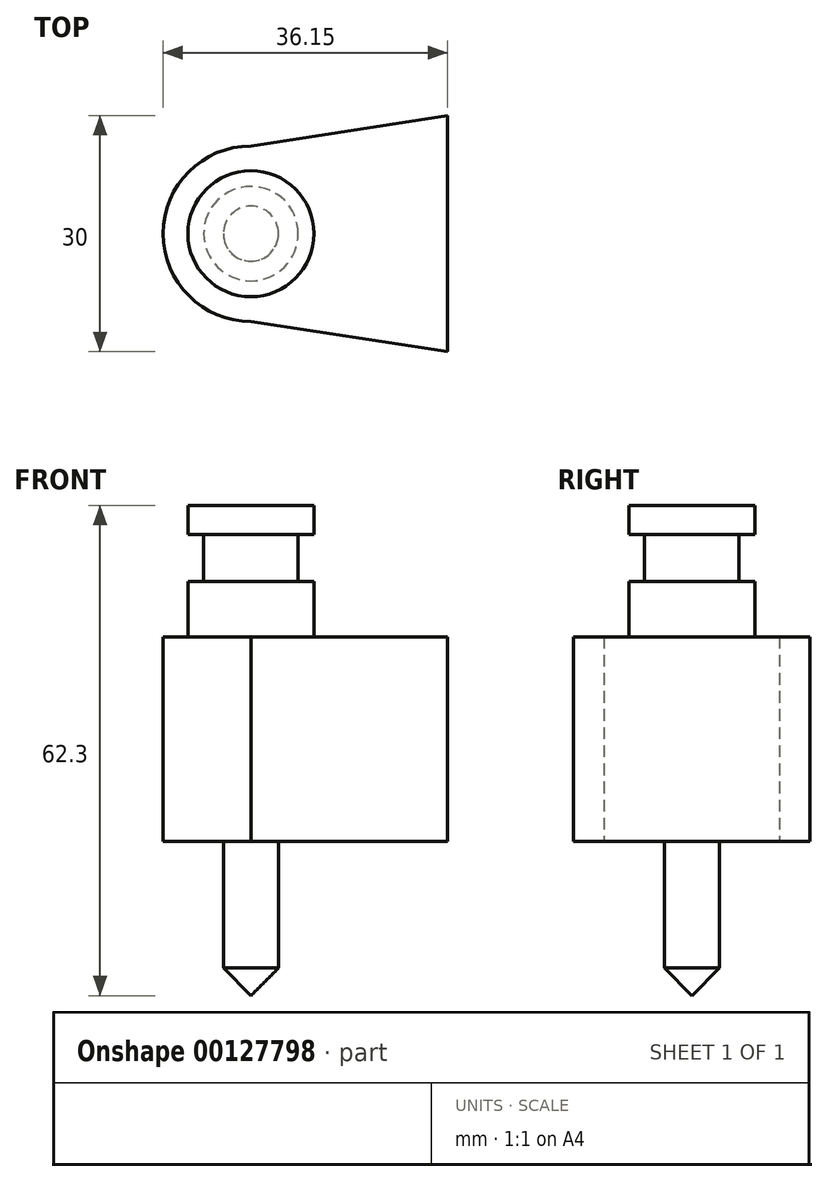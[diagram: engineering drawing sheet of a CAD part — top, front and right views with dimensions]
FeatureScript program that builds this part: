
annotation { "Feature Type Name" : "Feature", "Feature Type Description" : "" }
export const myFeature = defineFeature(function(context is Context, id is Id, definition is map)
    precondition{}
    {
        {
            var Q0;
            Q0=qCreatedBy(makeId("Front.planeOp"),FACE);
            var sketch = newSketch(context, id + "F0", { "sketchPlane" : qUnion([Q0])});
            skLineSegment(sketch, "E0", {"start": v(-8, 0) * mm, "end": v(-8, -3.7) * mm});
            skLineSegment(sketch, "E1", {"start": v(-8, -3.7) * mm, "end": v(-6, -3.7) * mm});
            skLineSegment(sketch, "E2", {"start": v(-6, -3.7) * mm, "end": v(-6, -9.7) * mm});
            skLineSegment(sketch, "E3", {"start": v(-6, -9.7) * mm, "end": v(-8, -9.7) * mm});
            skLineSegment(sketch, "E4", {"start": v(-8, -9.7) * mm, "end": v(-8, -12.7) * mm});
            skLineSegment(sketch, "E5", {"start": v(-8, 0) * mm, "end": v(0, 0) * mm});
            skLineSegment(sketch, "E6", {"start": v(0, 0) * mm, "end": v(0, 11.4) * mm, "construction": true});
            skLineSegment(sketch, "E7", {"start": v(-8, -12.7) * mm, "end": v(-8, -16.7) * mm});
            skLineSegment(sketch, "E8", {"start": v(-8, -16.7) * mm, "end": v(-11.15, -16.7) * mm});
            skLineSegment(sketch, "E9", {"start": v(-11.15, -16.7) * mm, "end": v(-11.15, -42.7) * mm});
            skLineSegment(sketch, "E10", {"start": v(-11.15, -42.7) * mm, "end": v(0, -42.7) * mm});
            skLineSegment(sketch, "E11", {"start": v(0, 0) * mm, "end": v(0, -42.7) * mm});
            skSolve(sketch);
        }
        {
            var Q0;
            Q0=makeQuery(id+"F0.imprint","IMPRINT",FACE,{"disambiguationData":[TD([[makeQuery(id+"F0.imprint","IMPRINT",EDGE,{"derivedFrom":sQuery(id+"F0.wireOp",EDGE,"E0")}),1.0]])]});
            var Q1;
            Q1=sQuery(id+"F0.wireOp",EDGE,"E11");
            revolve(context, id + "F1", {"entities" : qUnion([Q0]), "axis" : qUnion([Q1]), "revolveType" : RevolveType.FULL});
        }
        {
            var Q0;
            Q0=qCreatedBy(makeId("Front.planeOp"),FACE);
            var sketch = newSketch(context, id + "F2", { "sketchPlane" : qUnion([Q0])});
            skLineSegment(sketch, "E12", {"start": v(0, -42.7) * mm, "end": v(-3.5, -42.7) * mm});
            skLineSegment(sketch, "E13", {"start": v(-3.5, -42.7) * mm, "end": v(-3.5, -58.8) * mm});
            skLineSegment(sketch, "E14", {"start": v(-3.5, -58.8) * mm, "end": v(0, -62.3) * mm});
            skLineSegment(sketch, "E15", {"start": v(0, -62.3) * mm, "end": v(0, -42.7) * mm});
            skSolve(sketch);
        }
        {
            var Q0;
            Q0 = qSketchRegion(id + "F2", true);
            var Q1;
            Q1=sQuery(id+"F2.wireOp",EDGE,"E15");
            revolve(context, id + "F3", {"operationType" : NewBodyOperationType.ADD, "entities" : qUnion([Q0]), "axis" : qUnion([Q1]), "revolveType" : RevolveType.FULL});
        }
        {
            var Q0;
            Q0=makeQuery(id+"F1.opRevolve","SWEPT_FACE",FACE,{"disambiguationData":[OSD([sQuery(id+"F0.wireOp",EDGE,"E10")])]});
            var sketch = newSketch(context, id + "F4", { "sketchPlane" : qUnion([Q0])});
            skArc(sketch, "E16.0.0", {"start": v(0, -11.15) * mm, "mid": v(11.15, 0) * mm, "end": v(0, 11.15) * mm});
            skLineSegment(sketch, "E17", {"start": v(0, 11.15) * mm, "end": v(25, 15) * mm});
            skLineSegment(sketch, "E18", {"start": v(25, 15) * mm, "end": v(25, -15) * mm});
            skLineSegment(sketch, "E19", {"start": v(25, -15) * mm, "end": v(0, -11.15) * mm});
            skLineSegment(sketch, "E20", {"start": v(0, 0) * mm, "end": v(-21.57, 0) * mm, "construction": true});
            skSolve(sketch);
        }
        {
            var Q0;
            Q0 = qSketchRegion(id + "F4", true);
            var Q1;
            Q1=makeQuery(id+"F1.opRevolve","SWEPT_FACE",FACE,{"disambiguationData":[OSD([sQuery(id+"F0.wireOp",EDGE,"E8")])]});
            extrude(context, id + "F5", {"entities" : qUnion([Q0]), "operationType" : NewBodyOperationType.ADD, "endBound" : BoundingType.UP_TO_SURFACE, "oppositeDirection" : true, "endBoundEntityFace" : qUnion([Q1]), "depth" : 25 * mm});
        }
    });
